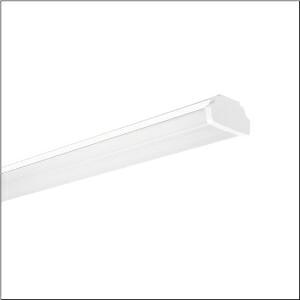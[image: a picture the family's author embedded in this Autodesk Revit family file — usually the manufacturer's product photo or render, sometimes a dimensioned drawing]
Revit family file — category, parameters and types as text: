
# Revit family: modario_r__31_gen_2_53bm812cv6c5d2_d13d
name_source: partatom
category: Lighting Fixtures
units: mm (PartAtom-declared; Revit-internal decimal feet)

## family parameters
Cut with Voids When Loaded = No
Host = Face
Light Source = No
Part Type = Normal
Room Calculation Point = No
Round Connector Dimension = Use Diameter
Shared = No

## types (1)
- --- (1 x LED, 12660 lm, 68.5 W, 6500K)
    Apparent Load = 69 VA
    CIE Flux Codes = 47 80 95 93 100
    Color Rendering = 80
    Color Temperature = 6500K
    Default Elevation = 1800 mm
    Description = Modario® 31 Gen.2, luminaire insert, of sheet steel, coil coated, white, length: 1.495mm, width: 81mm, height: 82mm, 5x system unit, system units: 299mm, LED rated luminous flux: 12.660lm, light colour: 865, control gear: ON/OFF Multilumen, CLOi, with plug, 3-pole, with phase selection, mains connection: 220..240V, AC, 50/60Hz, start of lifetime: 69W, end of service life: 82W, through-wiring accessed according to module size, primary optical cover: cover, of PMMA, light emission: direct distribution, primary light characteristic: symmetric, protection rating (complete): IP20, protection rating (LED compartment): IP50, insulation class (complete): insulation class I (protective earthing), certification: CE, ENEC, VDE, UKCA, impact resistance: IK03, permissible ambient temperature for indoor applications: -35..+35°C, corresponds to IFS (International Featured Standards) requirements for safety and quality in the food industry, reducing of maximum allowable ambient temperature of 5°C with ceiling mounting, IP40 when using the optional accessory 5TP9018, packaging unit: 1 piece
    Height = 92 mm
    Lamp = 1 x LED
    Lamp Light Flux = 12660 lm
    Lamp Power = 68.5 W
    Lamp count = 1
    Length = 1495 mm
    Luminous efficacy = 185 lm/W
    Manufacturer = Siteco
    ModVariant = No
    Model = 53BM812CV6C5D2
    Mounting Place = Ceiling
    Mounting Type = Pendant
    Number of Poles = 1
    OnlyDefault = Yes
    Power Factor = 1
    Product Name = Modario® 31 Gen.2
    Product group = luminaire insert
    ProductGroupID = 901
    Protection Class = Protection class I
    Protection Degree = IP 20
    RLX_Detail_Level = 1
    RLX_Emergency_Light_Flux = 0 lm
    RLX_Emergency_Type = 0
    RLX_Emergency_Type_DB = No
    RlxData = <blob elided: 40177 chars, md5=aa28f332>
    Socket = socket
    Standby Power = 0 W
    System Light Flux = 12660 lm
    System Power = 69 W
    Type Comments = factory setting: luminous flux: 100 % | (A | C | E) | 161 mA
    Type Image = l_1319597.jpg
    URL = http://relux.com
    VarID = @adj_010601
    Voltage = 0 V
    Weight = 0.00 kg
    Width = 81 mm

## geometry (parser evidence)
native form markers: Blend x4, Sweep x11
no freeform markers — native parametric forms only
